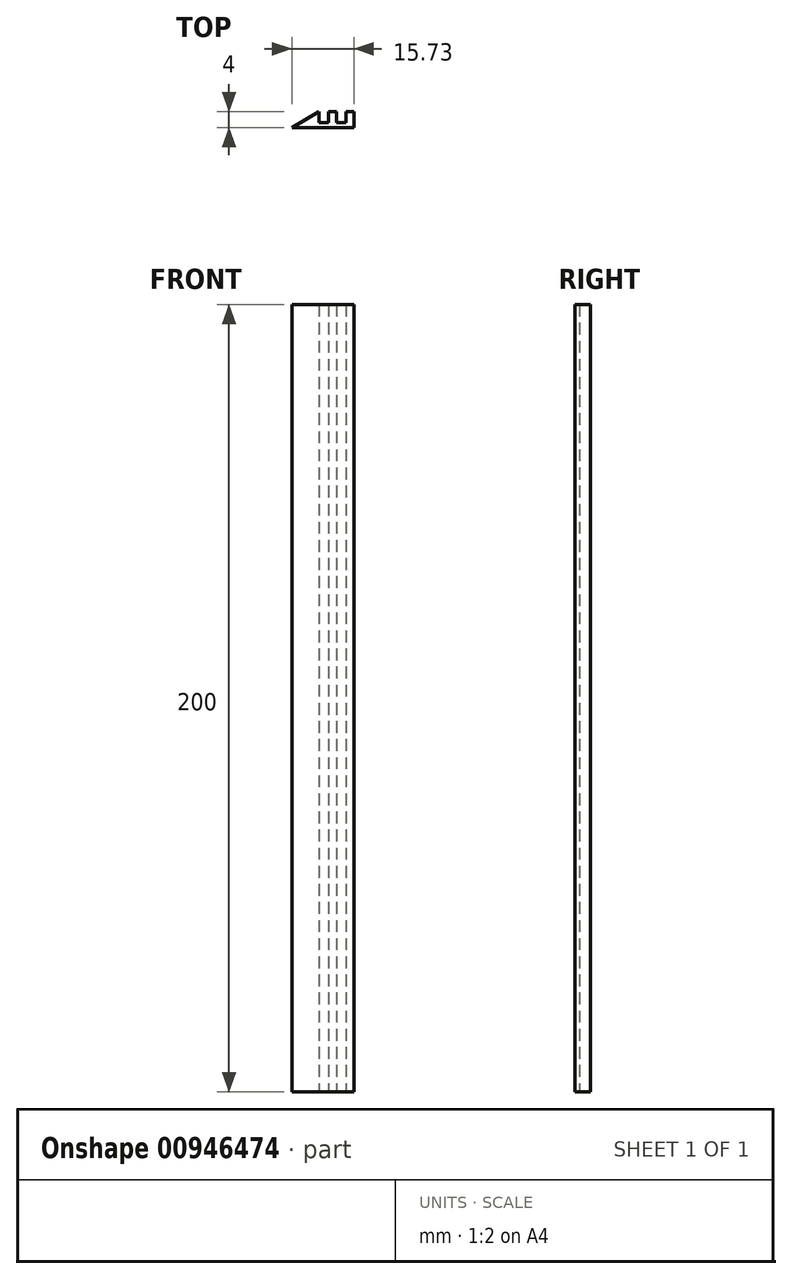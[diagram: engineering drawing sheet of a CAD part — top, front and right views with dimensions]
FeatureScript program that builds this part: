
annotation { "Feature Type Name" : "Feature", "Feature Type Description" : "" }
export const myFeature = defineFeature(function(context is Context, id is Id, definition is map)
    precondition{}
    {
        {
            var Q0;
            Q0=qCreatedBy(makeId("Top.planeOp"),FACE);
            var sketch = newSketch(context, id + "F0", { "sketchPlane" : qUnion([Q0])});
            skLineSegment(sketch, "E0", {"start": v(0, 0) * mm, "end": v(15.73, 0) * mm});
            skLineSegment(sketch, "E1", {"start": v(15.73, 0) * mm, "end": v(15.73, 4) * mm});
            skLineSegment(sketch, "E2", {"start": v(15.73, 4) * mm, "end": v(13.73, 4) * mm});
            skLineSegment(sketch, "E3", {"start": v(13.73, 4) * mm, "end": v(13.73, 1.2) * mm});
            skLineSegment(sketch, "E4", {"start": v(13.73, 1.2) * mm, "end": v(11.33, 1.2) * mm});
            skLineSegment(sketch, "E5", {"start": v(11.33, 1.2) * mm, "end": v(11.33, 4) * mm});
            skLineSegment(sketch, "E6", {"start": v(11.33, 4) * mm, "end": v(9.33, 4) * mm});
            skLineSegment(sketch, "E7", {"start": v(9.33, 4) * mm, "end": v(9.33, 1.2) * mm});
            skLineSegment(sketch, "E8", {"start": v(9.33, 1.2) * mm, "end": v(6.93, 1.2) * mm});
            skLineSegment(sketch, "E9", {"start": v(6.93, 1.2) * mm, "end": v(6.93, 4) * mm});
            skLineSegment(sketch, "E10", {"start": v(6.93, 4) * mm, "end": v(0, 0) * mm});
            skSolve(sketch);
        }
        {
            var Q0;
            Q0 = qSketchRegion(id + "F0", true);
            extrude(context, id + "F1", {"entities" : qUnion([Q0]), "depth" : 200 * mm, "offsetDistance" : 25 * mm});
        }
    });
